# Revit family: VENTS-TT_SILENT_M_EC
name_source: partatom
category: Mechanical Equipment
units: mm (PartAtom-declared; Revit-internal decimal feet)

## family parameters
Always vertical = No
Classification = None
Cut with Voids When Loaded = No
OmniClass Number = 23.75.35.17.11
OmniClass Title = Fans for Air Ductwork
Part Type = Breaks Into
Room Calculation Point = No
Round Connector Dimension = Use Diameter
Shared = No
Work Plane-Based = No

## types (7) — shared parameters
Description = Inline mixed-flow fan in sound- and heat-insulated casing for round ducts
Distribution Box Material = Distribution Box Dark Grey
ElBoxR = 15 mm  [stored 0.0492126 ft]
ElBoxType2 = Yes
Family Version = 1.0
Fan Material = Metal Black
Hanger Material = Metal Zinc
L22 = 8 mm  [stored 0.0262467 ft]
L23 = 13 mm
Load Classification = HVAC
Maintenance Zone Height = 600 mm
Maintenance Zone Length = 600 mm
Maintenance Zone Material = Maintenance Zone
Maintenance Zone Width = 600 mm
Manufacturer = Vents
Number of Poles = 1
Power Factor = 1
Protection rating = IPX4
Transported Air Temperature (°C) = -25...+55
URL = https://ventilation-system.com
Voltage = 230 V

## per-type parameters (varying)
- TT Silent-M 100 EC: Apparent Power=30 VA; Current=0 A; D=100 mm  [stored 0.328084 ft]; D1=214 mm; Dd12=3 mm  [stored 0.00984252 ft]; Dd13=4 mm  [stored 0.0131234 ft]; Dd14=39 mm  [stored 0.127953 ft]; Dd16=54 mm  [stored 0.177165 ft]; Dd22=3 mm  [stored 0.00984252 ft]; Dd23=4 mm  [stored 0.0131234 ft]; Dd24=39 mm  [stored 0.127953 ft]; Dd26=54 mm  [stored 0.177165 ft]; Duct Connection Size=100 mm  [stored 0.328084 ft]; ElBoxH=124 mm; ElBoxL=98 mm  [stored 0.321522 ft]; ElBoxType1=Yes; ElBoxW=116 mm; HangerBaseH=113 mm; HangerExtraL=Yes; HangerH=113 mm; HangerL=214 mm; HangerL1=214 mm; HangerW=93 mm  [stored 0.305118 ft]; L=505 mm; L1=25 mm  [stored 0.082021 ft]; L11=139 mm; L12=8 mm  [stored 0.0262467 ft]; L13=13 mm; L14=34 mm; L15=70 mm; L16=8 mm  [stored 0.0262467 ft]; L17=6 mm  [stored 0.019685 ft]; L2=25 mm  [stored 0.082021 ft]; L21=184 mm; L24=39 mm  [stored 0.127953 ft]; L25=110 mm; L26=8 mm  [stored 0.0262467 ft]; L27=6 mm  [stored 0.019685 ft]; Maintenance Zone Length Calc=600 mm; Maximum Air Flow=300 m³/h; Noise Level at 3 m (dBa)=37; Power=30 W; R1=107 mm  [stored 0.35105 ft]; RPM (min-1)=3680; Type Comments=Inline mixed-flow fan TT Silent-M 100 EC; Weight=4.90 kg
- TT Silent-M 125 EC: Apparent Power=40 VA; Current=0 A; D=125 mm; D1=214 mm; Dd12=3 mm  [stored 0.00984252 ft]; Dd13=4 mm  [stored 0.0131234 ft]; Dd14=28 mm  [stored 0.0918635 ft]; Dd16=41 mm  [stored 0.134514 ft]; Dd22=3 mm  [stored 0.00984252 ft]; Dd23=4 mm  [stored 0.0131234 ft]; Dd24=26 mm; Dd26=41 mm  [stored 0.134514 ft]; Duct Connection Size=125 mm; ElBoxH=124 mm; ElBoxL=98 mm  [stored 0.321522 ft]; ElBoxType1=Yes; ElBoxW=116 mm; HangerBaseH=113 mm; HangerExtraL=Yes; HangerH=113 mm; HangerL=214 mm; HangerL1=214 mm; HangerW=93 mm  [stored 0.305118 ft]; L=474 mm; L1=25 mm  [stored 0.082021 ft]; L11=123 mm; L12=8 mm  [stored 0.0262467 ft]; L13=13 mm; L14=24 mm  [stored 0.0787402 ft]; L15=64 mm  [stored 0.209974 ft]; L16=8 mm  [stored 0.0262467 ft]; L17=6 mm  [stored 0.019685 ft]; L2=25 mm  [stored 0.082021 ft]; L21=169 mm; L24=24 mm  [stored 0.0787402 ft]; L25=110 mm; L26=8 mm  [stored 0.0262467 ft]; L27=6 mm  [stored 0.019685 ft]; Maintenance Zone Length Calc=600 mm; Maximum Air Flow=450 m³/h; Noise Level at 3 m (dBa)=43; Power=40 W; R1=107 mm  [stored 0.35105 ft]; RPM (min-1)=3750; Type Comments=Inline mixed-flow fan TT Silent-M 125 EC; Weight=4.80 kg
- TT Silent-M 150 EC: Apparent Power=55 VA; Current=0 A; D=150 mm; D1=244 mm; Dd12=3 mm  [stored 0.00984252 ft]; Dd13=4 mm  [stored 0.0131234 ft]; Dd14=28 mm  [stored 0.0918635 ft]; Dd16=45 mm  [stored 0.147638 ft]; Dd22=3 mm  [stored 0.00984252 ft]; Dd23=4 mm  [stored 0.0131234 ft]; Dd24=22 mm  [stored 0.0721785 ft]; Dd26=44 mm  [stored 0.144357 ft]; Duct Connection Size=150 mm; ElBoxH=137 mm; ElBoxL=114 mm; ElBoxType1=Yes; ElBoxW=150 mm; HangerBaseH=126 mm; HangerExtraL=Yes; HangerH=126 mm; HangerL=244 mm; HangerL1=244 mm; HangerW=93 mm  [stored 0.305118 ft]; L=580 mm; L1=25 mm  [stored 0.082021 ft]; L11=163 mm; L12=8 mm  [stored 0.0262467 ft]; L13=13 mm; L14=19 mm  [stored 0.062336 ft]; L15=109 mm; L16=8 mm  [stored 0.0262467 ft]; L17=6 mm  [stored 0.019685 ft]; L2=25 mm  [stored 0.082021 ft]; L21=209 mm; L24=11 mm  [stored 0.0360892 ft]; L25=163 mm; L26=8 mm  [stored 0.0262467 ft]; L27=6 mm  [stored 0.019685 ft]; Maintenance Zone Length Calc=600 mm; Maximum Air Flow=600 m³/h; Noise Level at 3 m (dBa)=38; Power=55 W; R1=122 mm; RPM (min-1)=3390; Type Comments=Inline mixed-flow fan TT Silent-M 150 EC; Weight=6.00 kg
- TT Silent-M 160 EC: Apparent Power=55 VA; Current=0 A; D=160 mm; D1=244 mm; Dd12=3 mm  [stored 0.00984252 ft]; Dd13=5 mm  [stored 0.0164042 ft]; Dd14=23 mm  [stored 0.0754593 ft]; Dd16=39 mm  [stored 0.127953 ft]; Dd22=3 mm  [stored 0.00984252 ft]; Dd23=5 mm  [stored 0.0164042 ft]; Dd24=17 mm; Dd26=39 mm  [stored 0.127953 ft]; Duct Connection Size=160 mm; ElBoxH=137 mm; ElBoxL=114 mm; ElBoxType1=Yes; ElBoxW=150 mm; HangerBaseH=126 mm; HangerExtraL=Yes; HangerH=126 mm; HangerL=244 mm; HangerL1=244 mm; HangerW=93 mm  [stored 0.305118 ft]; L=580 mm; L1=25 mm  [stored 0.082021 ft]; L11=163 mm; L12=8 mm  [stored 0.0262467 ft]; L13=13 mm; L14=21 mm  [stored 0.0688976 ft]; L15=107 mm  [stored 0.35105 ft]; L16=8 mm  [stored 0.0262467 ft]; L17=6 mm  [stored 0.019685 ft]; L2=25 mm  [stored 0.082021 ft]; L21=209 mm; L24=11 mm  [stored 0.0360892 ft]; L25=163 mm; L26=8 mm  [stored 0.0262467 ft]; L27=6 mm  [stored 0.019685 ft]; Maintenance Zone Length Calc=600 mm; Maximum Air Flow=600 m³/h; Noise Level at 3 m (dBa)=38; Power=55 W; R1=122 mm; RPM (min-1)=3390; Type Comments=Inline mixed-flow fan TT Silent-M 160 EC; Weight=6.00 kg
- TT Silent-M 200 EC: Apparent Power=123 VA; Current=1 A; D=200 mm; D1=293 mm; Dd12=1 mm  [stored 0.00328084 ft]; Dd13=2 mm  [stored 0.00656168 ft]; Dd14=9 mm  [stored 0.0295276 ft]; Dd16=44 mm  [stored 0.144357 ft]; Dd22=4 mm  [stored 0.0131234 ft]; Dd23=5 mm  [stored 0.0164042 ft]; Dd24=27 mm  [stored 0.0885827 ft]; Dd26=44 mm  [stored 0.144357 ft]; Duct Connection Size=200 mm; ElBoxH=53 mm  [stored 0.173885 ft]; ElBoxL=104 mm; ElBoxType1=No; ElBoxW=104 mm; HangerBaseH=149 mm; HangerExtraL=No; HangerH=149 mm; HangerL=344 mm; HangerL1=275 mm; HangerW=135 mm; L=558 mm; L1=30 mm  [stored 0.0984252 ft]; L11=148 mm; L12=3 mm  [stored 0.00984252 ft]; L13=4 mm  [stored 0.0131234 ft]; L14=10 mm  [stored 0.0328084 ft]; L15=116 mm; L16=6 mm  [stored 0.019685 ft]; L17=9 mm  [stored 0.0295276 ft]; L2=30 mm  [stored 0.0984252 ft]; L21=179 mm; L24=21 mm  [stored 0.0688976 ft]; L25=122 mm; L26=6 mm  [stored 0.019685 ft]; L27=9 mm  [stored 0.0295276 ft]; Maintenance Zone Length Calc=600 mm; Maximum Air Flow=1040 m³/h; Noise Level at 3 m (dBa)=43; Power=123 W; R1=147 mm; RPM (min-1)=3390; Type Comments=Inline mixed-flow fan TT Silent-M 200 EC; Weight=8.60 kg
- TT Silent-M 250 EC: Apparent Power=169 VA; Current=1 A; D=250 mm; D1=358 mm; Dd12=1 mm  [stored 0.00328084 ft]; Dd13=2 mm  [stored 0.00656168 ft]; Dd14=6 mm  [stored 0.019685 ft]; Dd16=52 mm; Dd22=5 mm  [stored 0.0164042 ft]; Dd23=6 mm  [stored 0.019685 ft]; Dd24=30 mm  [stored 0.0984252 ft]; Dd26=52 mm; Duct Connection Size=250 mm; ElBoxH=53 mm  [stored 0.173885 ft]; ElBoxL=104 mm; ElBoxType1=No; ElBoxW=104 mm; HangerBaseH=182 mm; HangerExtraL=No; HangerH=182 mm; HangerL=402 mm; HangerL1=332 mm; HangerW=150 mm; L=664 mm; L1=32 mm  [stored 0.104987 ft]; L11=176 mm; L12=3 mm  [stored 0.00984252 ft]; L13=4 mm  [stored 0.0131234 ft]; L14=10 mm  [stored 0.0328084 ft]; L15=144 mm; L16=6 mm  [stored 0.019685 ft]; L17=9 mm  [stored 0.0295276 ft]; L2=32 mm  [stored 0.104987 ft]; L21=218 mm; L24=23 mm  [stored 0.0754593 ft]; L25=159 mm; L26=6 mm  [stored 0.019685 ft]; L27=9 mm  [stored 0.0295276 ft]; Maintenance Zone Length Calc=664 mm; Maximum Air Flow=1285 m³/h; Noise Level at 3 m (dBa)=42; Power=169 W; R1=179 mm; RPM (min-1)=2870; Type Comments=Inline mixed-flow fan TT Silent-M 250 EC; Weight=12.50 kg
- TT Silent-M 315 EC: Apparent Power=284 VA; Current=1 A; D=315 mm; D1=432 mm; Dd12=1 mm  [stored 0.00328084 ft]; Dd13=2 mm  [stored 0.00656168 ft]; Dd14=6 mm  [stored 0.019685 ft]; Dd16=55 mm  [stored 0.180446 ft]; Dd22=5 mm  [stored 0.0164042 ft]; Dd23=6 mm  [stored 0.019685 ft]; Dd24=30 mm  [stored 0.0984252 ft]; Dd26=52 mm; Duct Connection Size=315 mm; ElBoxH=53 mm  [stored 0.173885 ft]; ElBoxL=104 mm; ElBoxType1=No; ElBoxW=104 mm; HangerBaseH=219 mm; HangerExtraL=No; HangerH=219 mm; HangerL=478 mm; HangerL1=396 mm; HangerW=200 mm; L=785 mm; L1=32 mm  [stored 0.104987 ft]; L11=195 mm; L12=8 mm  [stored 0.0262467 ft]; L13=8 mm  [stored 0.0262467 ft]; L14=10 mm  [stored 0.0328084 ft]; L15=153 mm; L16=6 mm  [stored 0.019685 ft]; L17=10 mm  [stored 0.0328084 ft]; L2=32 mm  [stored 0.104987 ft]; L21=218 mm; L24=27 mm  [stored 0.0885827 ft]; L25=154 mm; L26=6 mm  [stored 0.019685 ft]; L27=10 mm  [stored 0.0328084 ft]; Maintenance Zone Length Calc=785 mm; Maximum Air Flow=1970 m³/h; Noise Level at 3 m (dBa)=46; Power=284 W; R1=216 mm; RPM (min-1)=2826; Type Comments=Inline mixed-flow fan TT Silent-M 315 EC; Weight=19.80 kg

note: column(s) folded — value = type name in every type: Model

note: [stored X ft] marks values corroborated as IEEE doubles in the binary element streams (Revit-internal decimal feet)

## geometry (parser evidence)
native form markers: Sweep x9
no freeform markers — native parametric forms only
